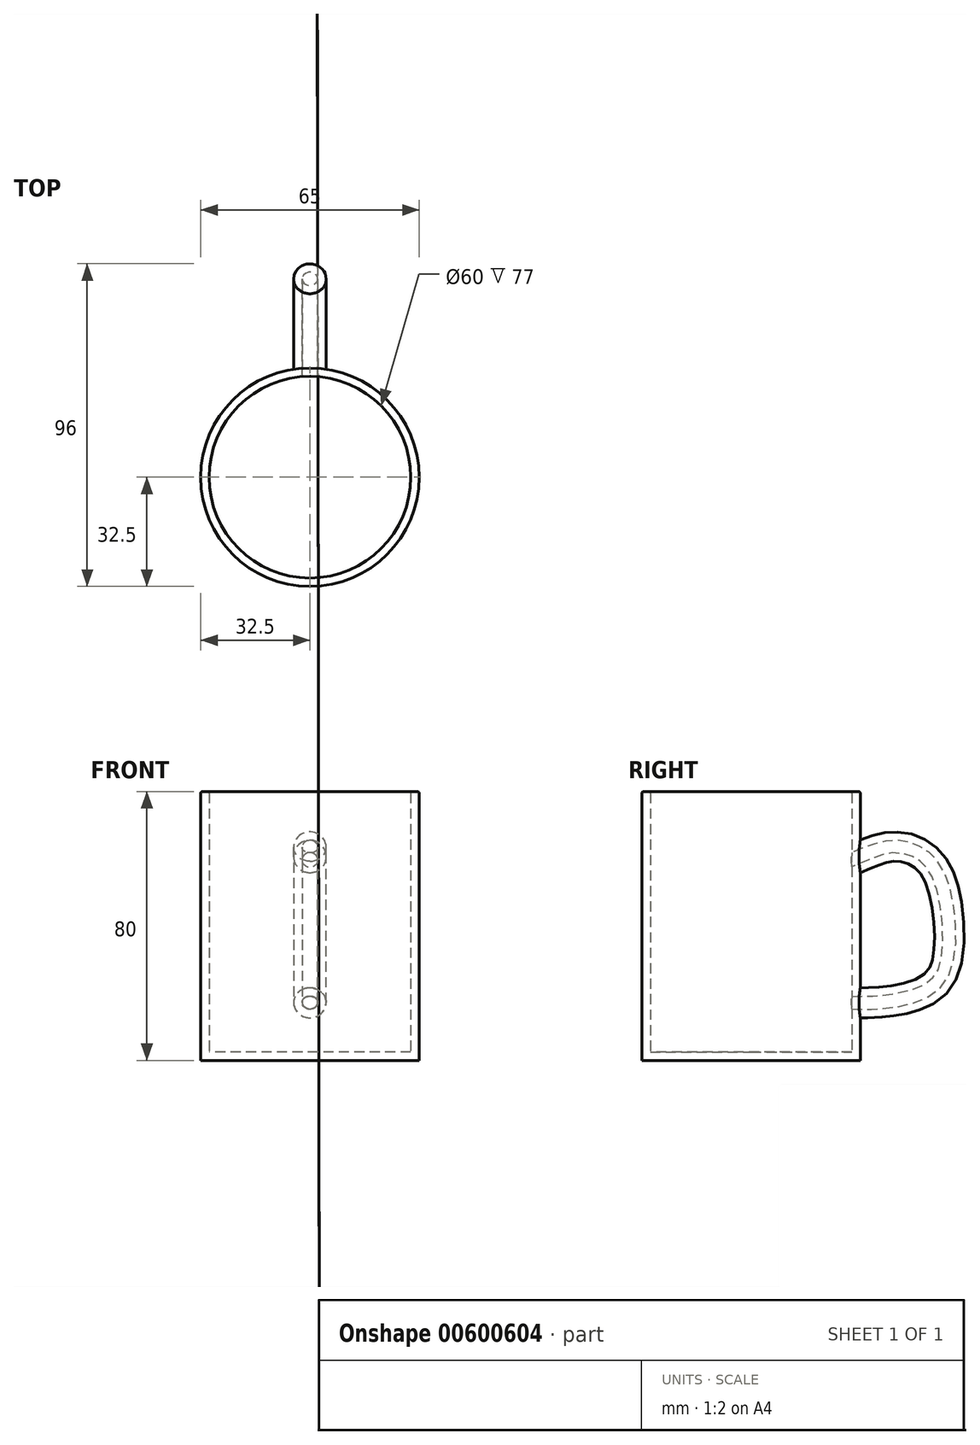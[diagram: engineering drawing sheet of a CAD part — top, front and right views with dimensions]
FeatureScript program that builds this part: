
annotation { "Feature Type Name" : "Feature", "Feature Type Description" : "" }
export const myFeature = defineFeature(function(context is Context, id is Id, definition is map)
    precondition{}
    {
        {
            var Q0;
            Q0=qCreatedBy(makeId("Top.planeOp"),FACE);
            var sketch = newSketch(context, id + "F0", { "sketchPlane" : qUnion([Q0])});
            skCircle(sketch, "E0", {"center": v(0, 0) * mm, "radius": 32.5 * mm});
            skSolve(sketch);
        }
        {
            var Q0;
            Q0 = qSketchRegion(id + "F0", true);
            extrude(context, id + "F1", {"entities" : qUnion([Q0]), "depth" : 80 * mm, "offsetDistance" : 25 * mm});
        }
        {
            var Q0;
            Q0=qCreatedBy(makeId("Right.planeOp"),FACE);
            var sketch = newSketch(context, id + "F2", { "sketchPlane" : qUnion([Q0])});
            skFitSpline(sketch, "E1", {"points": [v(31, 61.87) * mm, v(43.23, 65.07) * mm, v(54.3, 60.12) * mm, v(60.12, 44.4) * mm, v(56.92, 22.85) * mm, v(40.03, 15.87) * mm, v(28.21, 16) * mm], "startDerivative": vector(78.06, 31.8) * mm, "endDerivative": vector(-54.85, 9.93) * mm});
            skSolve(sketch);
        }
        {
            var Q0;
            Q0=qCreatedBy(makeId("Front.planeOp"),FACE);
            cPlane(context, id + "F3", {"entities" : qUnion([Q0]), "cplaneType" : CPlaneType.OFFSET, "offset" : 32.5 * mm, "oppositeDirection" : true, "width" : 150 * mm, "height" : 150 * mm});
        }
        {
            var Q0;
            Q0=qCreatedBy(id+"F3.planeOp",FACE);
            var sketch = newSketch(context, id + "F4", { "sketchPlane" : qUnion([Q0])});
            skCircle(sketch, "E2", {"center": v(0, 60.72) * mm, "radius": 4.84 * mm});
            skSolve(sketch);
        }
        {
            var Q0;
            Q0=makeQuery(id+"F4.imprint","IMPRINT",FACE,{"disambiguationData":[TD([[makeQuery(id+"F4.imprint","IMPRINT",EDGE,{"derivedFrom":sQuery(id+"F4.wireOp",EDGE,"E2")}),1.0]])]});
            var Q1;
            Q1=sQuery(id+"F2.wireOp",EDGE,"E1");
            sweep(context, id + "F5", {"operationType" : NewBodyOperationType.ADD, "profiles" : qUnion([Q0]), "path" : qUnion([Q1])});
        }
        {
            var Q0;
            Q0=makeQuery(id+"F1.opExtrude","CAP_FACE",FACE,{"disambiguationData":[OSD([sQuery(id+"F0.wireOp",EDGE,"E0")])],"isStart":false});
            shell(context, id + "F6", {"entities" : qUnion([Q0]), "thickness" : 2.5 * mm});
        }
        {
            var Q0;
            {var subQ0=sQuery(id+"F0.wireOp",EDGE,"E0");Q0=makeQuery(id+"F6.opShell","OFFSET_EDGE",EDGE,{"disambiguationData":[OSD([subQ0]),TDD([makeQuery(id+"F1.opExtrude","CAP_EDGE",EDGE,{"disambiguationData":[OSD([subQ0])],"isStart":false})])]});}
            var Q1;
            Q1=makeQuery(id+"F1.opExtrude","CAP_EDGE",EDGE,{"disambiguationData":[OSD([sQuery(id+"F0.wireOp",EDGE,"E0")])],"isStart":false});
            fillet(context, id + "F7", {"entities" : qUnion([Q0, Q1]), "radius" : 0.5 * mm, "tangentPropagation" : true, "allowEdgeOverflow" : false});
        }
    });
